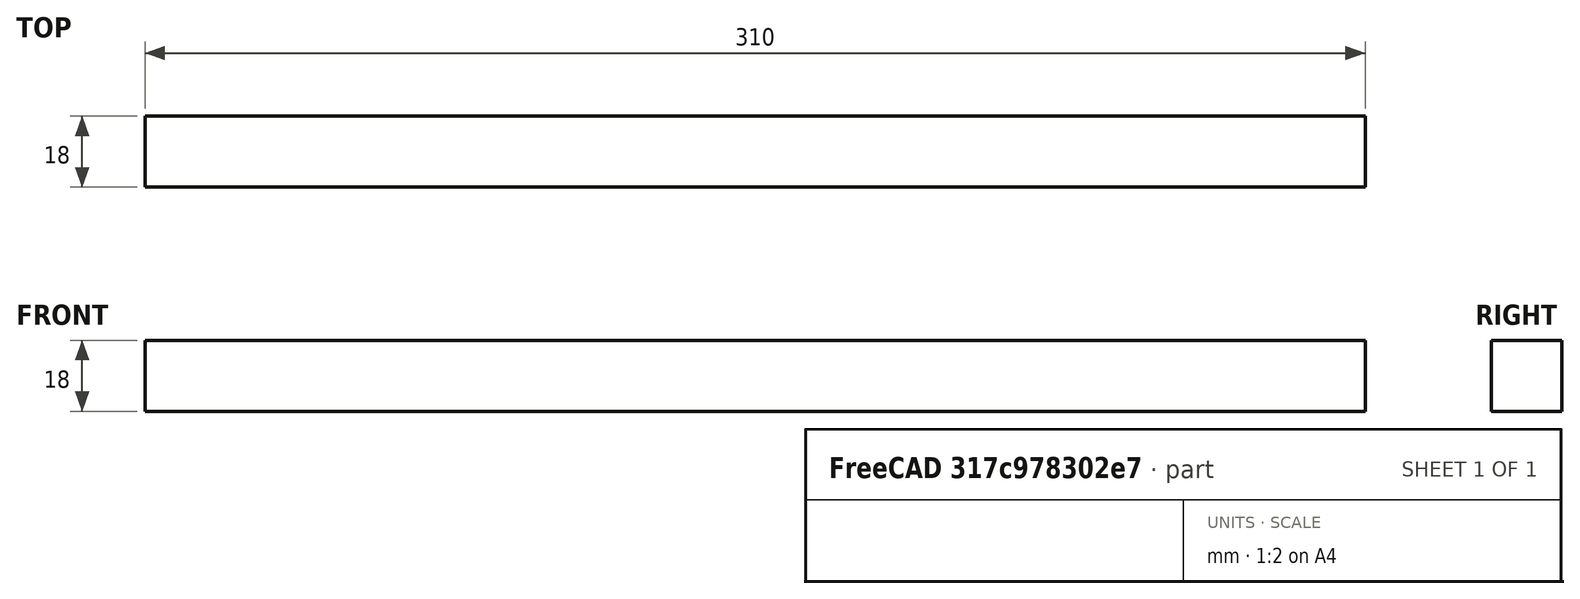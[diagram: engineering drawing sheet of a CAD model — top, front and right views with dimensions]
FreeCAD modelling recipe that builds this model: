
FCSTD DOCUMENT  (FreeCAD 0.19R24291 (Git))
Label: 3000_strut_x_18_18_400
License: All rights reserved
LicenseURL: http://en.wikipedia.org/wiki/All_rights_reserved
objects: Sketcher::SketchObject×1, PartDesign::Pad×1, PartDesign::Body×1
note: 4 computed .brp shape members not serialized (recipe doc carries the construction recipe); baked Part::Feature solids carry a one-line shape summary decoded from their .brp

FEATURE [Sketcher::SketchObject] Sketch
  FullyConstrained = true
  MapMode = 5
  Placement = pos=(0,0,0) rot=(0.57735,0.57735,0.57735;2.0944rad)
  Support = -> [YZ_Plane]
  sketch-geometry (4):
    g0: LineSegment StartX=0 StartY=18 StartZ=0 EndX=18 EndY=18 EndZ=0
    g1: LineSegment StartX=18 StartY=18 StartZ=0 EndX=18 EndY=0 EndZ=0
    g2: LineSegment StartX=18 StartY=0 StartZ=0 EndX=0 EndY=0 EndZ=0
    g3: LineSegment StartX=0 StartY=0 StartZ=0 EndX=0 EndY=18 EndZ=0
  constraints (12):
    c: Coincident(g0,g1)
    c: Coincident(g1,g2)
    c: Coincident(g2,g3)
    c: Coincident(g3,g0)
    c: Horizontal(g0)
    c: Horizontal(g2)
    c: Vertical(g1)
    c: Vertical(g3)
    c: PointOnObject(g0,g-2)
    c: PointOnObject(g1,g-1)
    c: Equal(g1,g0)
    c: DistanceY(g1,g1) = 18
FEATURE [PartDesign::Pad] Pad
  Direction = (1,1,1)
  Length = 310
  Length2 = 100
  Placement = pos=(0,0,0) rot=(0.57735,0.57735,0.57735;2.0944rad)
  Profile = -> Sketch
  Type = 0
  expr: Length = 310
FEATURE [PartDesign::Body] Body
  Group = -> [Sketch,Pad]
  Origin = -> Origin
  Tip = -> Pad
